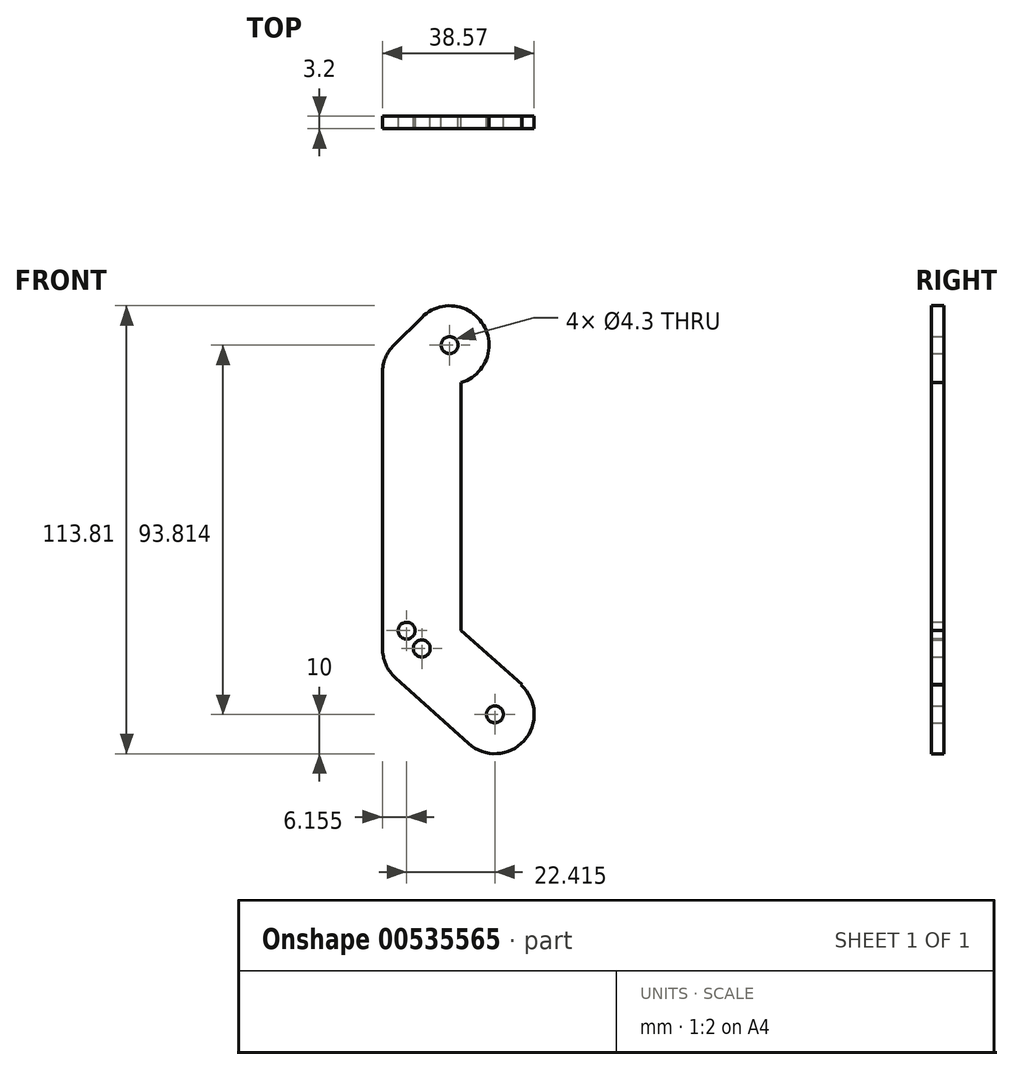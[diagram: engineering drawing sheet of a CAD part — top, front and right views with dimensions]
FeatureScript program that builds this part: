
annotation { "Feature Type Name" : "Feature", "Feature Type Description" : "" }
export const myFeature = defineFeature(function(context is Context, id is Id, definition is map)
    precondition{}
    {
        {
            var Q0;
            Q0=qCreatedBy(makeId("Front.planeOp"),FACE);
            var sketch = newSketch(context, id + "F0", { "sketchPlane" : qUnion([Q0])});
            skLineSegment(sketch, "E0", {"start": v(0, 0) * mm, "end": v(-18.57, 16.74) * mm});
            skLineSegment(sketch, "E1", {"start": v(-18.57, 16.74) * mm, "end": v(-18.57, 86.74) * mm});
            skCircle(sketch, "E2", {"center": v(-18.57, 86.74) * mm, "radius": 10 * mm});
            skCircle(sketch, "E3", {"center": v(-18.57, 16.74) * mm, "radius": 10 * mm});
            skCircle(sketch, "E4", {"center": v(0, 0) * mm, "radius": 10 * mm});
            skLineSegment(sketch, "E5", {"start": v(6.9, 7.65) * mm, "end": v(-6.7, -7.43) * mm});
            skLineSegment(sketch, "E6", {"start": v(-28.57, 86.74) * mm, "end": v(-8.57, 86.74) * mm});
            skLineSegment(sketch, "E7", {"start": v(-28.57, 16.74) * mm, "end": v(-8.57, 16.74) * mm});
            skLineSegment(sketch, "E8", {"start": v(-11.87, 24.17) * mm, "end": v(-25.26, 9.32) * mm});
            skLineSegment(sketch, "E9", {"start": v(-25.26, 9.32) * mm, "end": v(-6.7, -7.43) * mm});
            skLineSegment(sketch, "E10", {"start": v(-28.57, 86.74) * mm, "end": v(-28.57, 16.74) * mm});
            skLineSegment(sketch, "E11", {"start": v(-8.57, 86.74) * mm, "end": v(-8.57, 16.74) * mm});
            skLineSegment(sketch, "E12", {"start": v(-11.87, 24.17) * mm, "end": v(6.9, 7.65) * mm});
            skCircle(sketch, "E13", {"center": v(-11.5, 93.81) * mm, "radius": 10 * mm});
            skLineSegment(sketch, "E14", {"start": v(-11.5, 93.81) * mm, "end": v(-18.57, 86.74) * mm});
            skLineSegment(sketch, "E15", {"start": v(-25.64, 93.81) * mm, "end": v(-18.57, 100.89) * mm});
            skCircle(sketch, "E16", {"center": v(-18.57, 16.74) * mm, "radius": 2.15 * mm});
            skCircle(sketch, "E17", {"center": v(0, 0) * mm, "radius": 2.15 * mm});
            skCircle(sketch, "E18", {"center": v(-11.5, 93.81) * mm, "radius": 2.15 * mm});
            skSolve(sketch);
        }
        {
            var Q0;
            {var subQ0=sQuery(id+"F0.wireOp",EDGE,"E15");Q0=makeQuery(id+"F0.imprint","IMPRINT",FACE,{"disambiguationData":[TD([[makeQuery(id+"F0.imprint","IMPRINT",EDGE,{"derivedFrom":subQ0}),-1.0]])]});}
            var Q1;
            {var subQ5=sQuery(id+"F0.wireOp",EDGE,"E9");Q1=makeQuery(id+"F0.imprint","IMPRINT",FACE,{"disambiguationData":[TD([[makeQuery(id+"F0.imprint","IMPRINT",EDGE,{"derivedFrom":subQ5}),1.0]])]});}
            var Q2;
            {var subQ5=sQuery(id+"F0.wireOp",EDGE,"E10");Q2=makeQuery(id+"F0.imprint","IMPRINT",FACE,{"disambiguationData":[TD([[makeQuery(id+"F0.imprint","IMPRINT",EDGE,{"derivedFrom":subQ5}),1.0]])]});}
            var Q3;
            {var subQ1=sQuery(id+"F0.wireOp",EDGE,"E1");var subQ3=sQuery(id+"F0.wireOp",EDGE,"E2");var subQ4=makeQuery(id+"F0.imprint","INTERSECT",VERTEX,{"derivedFrom":[subQ1,subQ3]});Q3=makeQuery(id+"F0.imprint","IMPRINT",FACE,{"disambiguationData":[TD([[makeQuery(id+"F0.imprint","IMPRINT",EDGE,{"disambiguationData":[TD([[subQ4,1.0]])],"derivedFrom":subQ3}),1.0]])]});}
            var Q4;
            {var subQ0=sQuery(id+"F0.wireOp",EDGE,"E2");var subQ1=makeQuery(id+"F0.imprint","INTERSECT",VERTEX,{"derivedFrom":[subQ0,sQuery(id+"F0.wireOp",EDGE,"E15")]});Q4=makeQuery(id+"F0.imprint","IMPRINT",FACE,{"disambiguationData":[TD([[makeQuery(id+"F0.imprint","IMPRINT",EDGE,{"disambiguationData":[TD([[subQ1,1.0]])],"derivedFrom":subQ0}),1.0]])]});}
            var Q5;
            {var subQ0=sQuery(id+"F0.wireOp",EDGE,"E11");var subQ3=sQuery(id+"F0.wireOp",EDGE,"E13");var subQ5=makeQuery(id+"F0.imprint","INTERSECT",VERTEX,{"derivedFrom":[subQ0,subQ3]});Q5=makeQuery(id+"F0.imprint","IMPRINT",FACE,{"disambiguationData":[TD([[makeQuery(id+"F0.imprint","IMPRINT",EDGE,{"disambiguationData":[TD([[subQ5,1.0]])],"derivedFrom":subQ3}),1.0]])]});}
            var Q6;
            {var subQ0=sQuery(id+"F0.wireOp",EDGE,"E11");var subQ3=sQuery(id+"F0.wireOp",EDGE,"E12");var subQ5=makeQuery(id+"F0.imprint","INTERSECT",VERTEX,{"derivedFrom":[subQ0,subQ3]});Q6=makeQuery(id+"F0.imprint","IMPRINT",FACE,{"disambiguationData":[TD([[makeQuery(id+"F0.imprint","IMPRINT",EDGE,{"disambiguationData":[TD([[subQ5,-1.0]])],"derivedFrom":subQ0}),-1.0]])]});}
            var Q7;
            {var subQ0=sQuery(id+"F0.wireOp",EDGE,"E7");var subQ5=sQuery(id+"F0.wireOp",EDGE,"E16");var subQ7=makeQuery(id+"F0.imprint","INTERSECT",VERTEX,{"disambiguationData":[OD(0.0)],"derivedFrom":[subQ0,subQ5]});Q7=makeQuery(id+"F0.imprint","IMPRINT",FACE,{"disambiguationData":[TD([[makeQuery(id+"F0.imprint","IMPRINT",EDGE,{"disambiguationData":[TD([[subQ7,-1.0]])],"derivedFrom":subQ5}),-1.0]])]});}
            var Q8;
            {var subQ0=sQuery(id+"F0.wireOp",EDGE,"E5");var subQ1=sQuery(id+"F0.wireOp",EDGE,"E4");var subQ3=makeQuery(id+"F0.imprint","INTERSECT",VERTEX,{"derivedFrom":[subQ1,subQ0]});Q8=makeQuery(id+"F0.imprint","IMPRINT",FACE,{"disambiguationData":[TD([[makeQuery(id+"F0.imprint","IMPRINT",EDGE,{"disambiguationData":[TD([[subQ3,-1.0]])],"derivedFrom":subQ0}),1.0]])]});}
            var Q9;
            {var subQ0=sQuery(id+"F0.wireOp",EDGE,"E17");var subQ1=sQuery(id+"F0.wireOp",EDGE,"E0");var subQ2=makeQuery(id+"F0.imprint","INTERSECT",VERTEX,{"derivedFrom":[subQ1,subQ0]});Q9=makeQuery(id+"F0.imprint","IMPRINT",FACE,{"disambiguationData":[TD([[makeQuery(id+"F0.imprint","IMPRINT",EDGE,{"disambiguationData":[TD([[subQ2,-1.0]])],"derivedFrom":subQ1}),-1.0]])]});}
            var Q10;
            {var subQ0=sQuery(id+"F0.wireOp",EDGE,"E17");var subQ1=sQuery(id+"F0.wireOp",EDGE,"E0");var subQ2=makeQuery(id+"F0.imprint","INTERSECT",VERTEX,{"derivedFrom":[subQ1,subQ0]});Q10=makeQuery(id+"F0.imprint","IMPRINT",FACE,{"disambiguationData":[TD([[makeQuery(id+"F0.imprint","IMPRINT",EDGE,{"disambiguationData":[TD([[subQ2,-1.0]])],"derivedFrom":subQ1}),1.0]])]});}
            var Q11;
            {var subQ1=sQuery(id+"F0.wireOp",EDGE,"E4");var subQ3=sQuery(id+"F0.wireOp",EDGE,"E0");var subQ4=makeQuery(id+"F0.imprint","INTERSECT",VERTEX,{"derivedFrom":[subQ3,subQ1]});Q11=makeQuery(id+"F0.imprint","IMPRINT",FACE,{"disambiguationData":[TD([[makeQuery(id+"F0.imprint","IMPRINT",EDGE,{"disambiguationData":[TD([[subQ4,-1.0]])],"derivedFrom":subQ3}),-1.0]])]});}
            var Q12;
            {var subQ0=sQuery(id+"F0.wireOp",EDGE,"E3");var subQ1=sQuery(id+"F0.wireOp",EDGE,"E0");var subQ2=makeQuery(id+"F0.imprint","INTERSECT",VERTEX,{"derivedFrom":[subQ1,subQ0]});Q12=makeQuery(id+"F0.imprint","IMPRINT",FACE,{"disambiguationData":[TD([[makeQuery(id+"F0.imprint","IMPRINT",EDGE,{"disambiguationData":[TD([[subQ2,-1.0]])],"derivedFrom":subQ1}),1.0]])]});}
            var Q13;
            {var subQ0=sQuery(id+"F0.wireOp",EDGE,"E16");var subQ1=sQuery(id+"F0.wireOp",EDGE,"E1");var subQ2=makeQuery(id+"F0.imprint","INTERSECT",VERTEX,{"derivedFrom":[subQ1,subQ0]});Q13=makeQuery(id+"F0.imprint","IMPRINT",FACE,{"disambiguationData":[TD([[makeQuery(id+"F0.imprint","IMPRINT",EDGE,{"disambiguationData":[TD([[subQ2,-1.0]])],"derivedFrom":subQ1}),1.0]])]});}
            var Q14;
            {var subQ0=sQuery(id+"F0.wireOp",EDGE,"E18");var subQ1=sQuery(id+"F0.wireOp",EDGE,"E2");var subQ2=makeQuery(id+"F0.imprint","INTERSECT",VERTEX,{"disambiguationData":[OD(1.0)],"derivedFrom":[subQ1,subQ0]});Q14=makeQuery(id+"F0.imprint","IMPRINT",FACE,{"disambiguationData":[TD([[makeQuery(id+"F0.imprint","IMPRINT",EDGE,{"disambiguationData":[TD([[subQ2,-1.0]])],"derivedFrom":subQ1}),-1.0]])]});}
            var Q15;
            {var subQ5=sQuery(id+"F0.wireOp",EDGE,"E3");var subQ7=sQuery(id+"F0.wireOp",EDGE,"E1");var subQ8=makeQuery(id+"F0.imprint","INTERSECT",VERTEX,{"derivedFrom":[subQ7,subQ5]});Q15=makeQuery(id+"F0.imprint","IMPRINT",FACE,{"disambiguationData":[TD([[makeQuery(id+"F0.imprint","IMPRINT",EDGE,{"disambiguationData":[TD([[subQ8,-1.0]])],"derivedFrom":subQ7}),-1.0]])]});}
            var Q16;
            {var subQ0=sQuery(id+"F0.wireOp",EDGE,"E16");var subQ1=sQuery(id+"F0.wireOp",EDGE,"E1");var subQ2=makeQuery(id+"F0.imprint","INTERSECT",VERTEX,{"derivedFrom":[subQ1,subQ0]});Q16=makeQuery(id+"F0.imprint","IMPRINT",FACE,{"disambiguationData":[TD([[makeQuery(id+"F0.imprint","IMPRINT",EDGE,{"disambiguationData":[TD([[subQ2,-1.0]])],"derivedFrom":subQ1}),-1.0]])]});}
            var Q17;
            {var subQ0=sQuery(id+"F0.wireOp",EDGE,"E7");var subQ5=sQuery(id+"F0.wireOp",EDGE,"E16");var subQ7=makeQuery(id+"F0.imprint","INTERSECT",VERTEX,{"disambiguationData":[OD(1.0)],"derivedFrom":[subQ0,subQ5]});Q17=makeQuery(id+"F0.imprint","IMPRINT",FACE,{"disambiguationData":[TD([[makeQuery(id+"F0.imprint","IMPRINT",EDGE,{"disambiguationData":[TD([[subQ7,-1.0]])],"derivedFrom":subQ5}),-1.0]])]});}
            var Q18;
            {var subQ0=sQuery(id+"F0.wireOp",EDGE,"E3");var subQ1=sQuery(id+"F0.wireOp",EDGE,"E0");var subQ2=makeQuery(id+"F0.imprint","INTERSECT",VERTEX,{"derivedFrom":[subQ1,subQ0]});Q18=makeQuery(id+"F0.imprint","IMPRINT",FACE,{"disambiguationData":[TD([[makeQuery(id+"F0.imprint","IMPRINT",EDGE,{"disambiguationData":[TD([[subQ2,-1.0]])],"derivedFrom":subQ1}),-1.0]])]});}
            var Q19;
            {var subQ0=sQuery(id+"F0.wireOp",EDGE,"E18");var subQ1=sQuery(id+"F0.wireOp",EDGE,"E2");var subQ2=makeQuery(id+"F0.imprint","INTERSECT",VERTEX,{"disambiguationData":[OD(1.0)],"derivedFrom":[subQ1,subQ0]});Q19=makeQuery(id+"F0.imprint","IMPRINT",FACE,{"disambiguationData":[TD([[makeQuery(id+"F0.imprint","IMPRINT",EDGE,{"disambiguationData":[TD([[subQ2,-1.0]])],"derivedFrom":subQ1}),1.0]])]});}
            var Q20;
            {var subQ1=sQuery(id+"F0.wireOp",EDGE,"E2");var subQ3=sQuery(id+"F0.wireOp",EDGE,"E18");var subQ4=makeQuery(id+"F0.imprint","INTERSECT",VERTEX,{"disambiguationData":[OD(0.0)],"derivedFrom":[subQ1,subQ3]});Q20=makeQuery(id+"F0.imprint","IMPRINT",FACE,{"disambiguationData":[TD([[makeQuery(id+"F0.imprint","IMPRINT",EDGE,{"disambiguationData":[TD([[subQ4,1.0]])],"derivedFrom":subQ3}),-1.0]])]});}
            var Q21;
            {var subQ1=sQuery(id+"F0.wireOp",EDGE,"E1");var subQ3=sQuery(id+"F0.wireOp",EDGE,"E2");var subQ4=makeQuery(id+"F0.imprint","INTERSECT",VERTEX,{"derivedFrom":[subQ1,subQ3]});Q21=makeQuery(id+"F0.imprint","IMPRINT",FACE,{"disambiguationData":[TD([[makeQuery(id+"F0.imprint","IMPRINT",EDGE,{"disambiguationData":[TD([[subQ4,-1.0]])],"derivedFrom":subQ3}),1.0]])]});}
            var Q22;
            {var subQ1=sQuery(id+"F0.wireOp",EDGE,"E2");var subQ3=sQuery(id+"F0.wireOp",EDGE,"E13");var subQ4=makeQuery(id+"F0.imprint","INTERSECT",VERTEX,{"disambiguationData":[OD(1.0)],"derivedFrom":[subQ1,subQ3]});Q22=makeQuery(id+"F0.imprint","IMPRINT",FACE,{"disambiguationData":[TD([[makeQuery(id+"F0.imprint","IMPRINT",EDGE,{"disambiguationData":[TD([[subQ4,-1.0]])],"derivedFrom":subQ1}),1.0]])]});}
            extrude(context, id + "F1", {"entities" : qUnion([Q0, Q1, Q2, Q3, Q4, Q5, Q6, Q7, Q8, Q9, Q10, Q11, Q12, Q13, Q14, Q15, Q16, Q17, Q18, Q19, Q20, Q21, Q22]), "depth" : 3.2 * mm, "offsetDistance" : 25 * mm});
        }
        {
            var Q0;
            Q0=qCreatedBy(makeId("Front.planeOp"),FACE);
            var sketch = newSketch(context, id + "F2", { "sketchPlane" : qUnion([Q0])});
            skCircle(sketch, "E19", {"center": v(-22.42, 21.26) * mm, "radius": 2.15 * mm});
            skSolve(sketch);
        }
        {
            var Q0;
            Q0 = qSketchRegion(id + "F2", true);
            extrude(context, id + "F3", {"entities" : qUnion([Q0]), "operationType" : NewBodyOperationType.REMOVE, "oppositeDirection" : true, "depth" : 25 * mm, "offsetDistance" : 25 * mm, "symmetric" : true});
        }
    });
